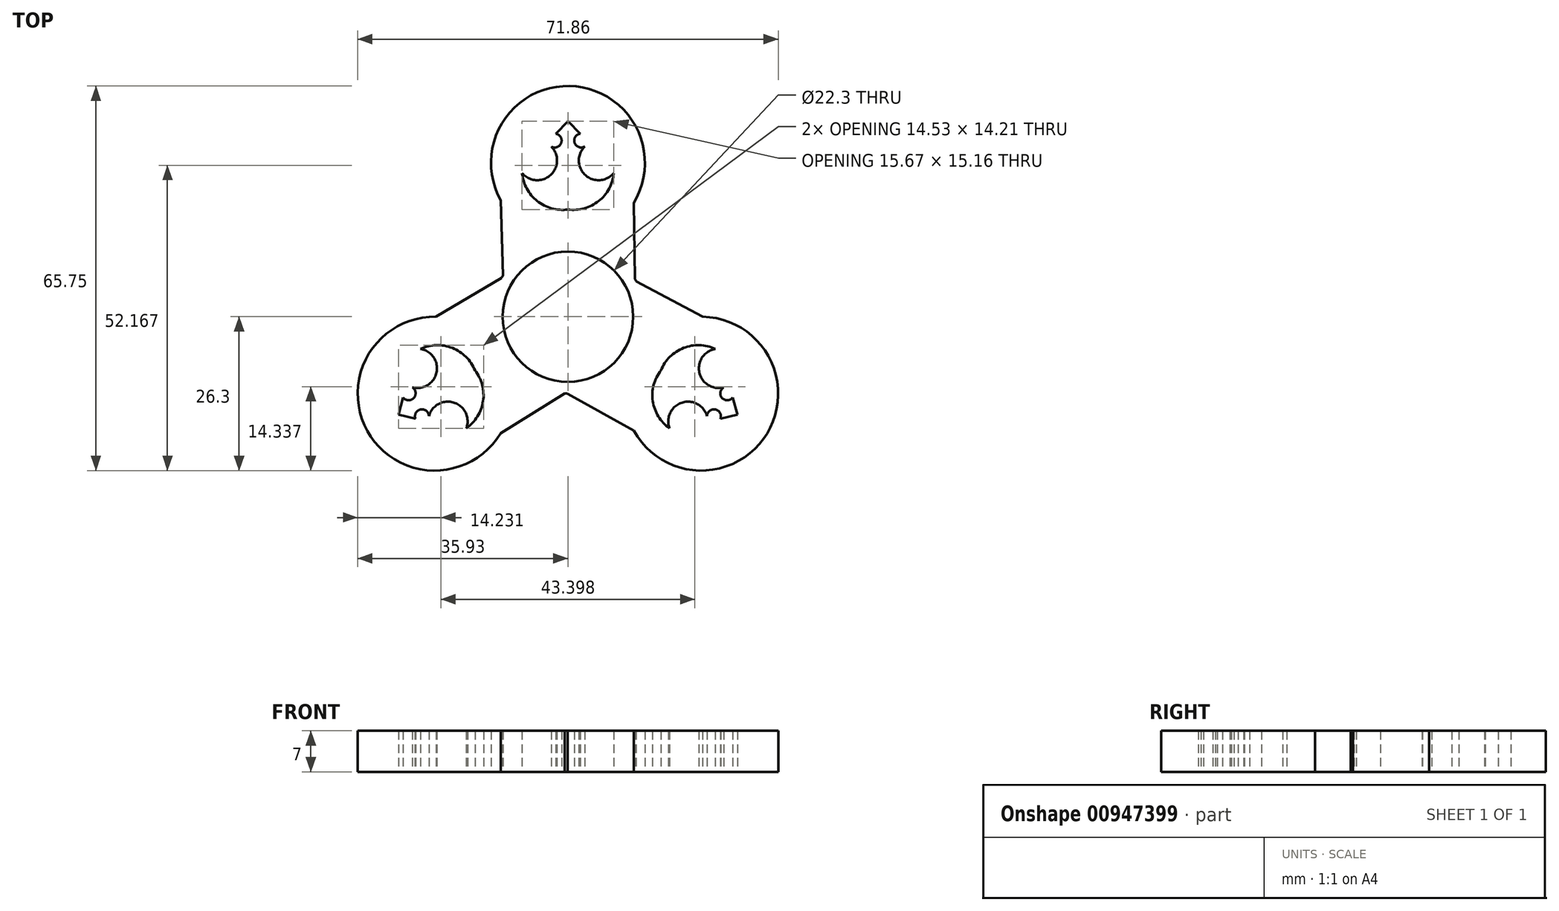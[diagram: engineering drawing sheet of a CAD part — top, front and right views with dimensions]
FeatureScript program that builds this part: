
annotation { "Feature Type Name" : "Feature", "Feature Type Description" : "" }
export const myFeature = defineFeature(function(context is Context, id is Id, definition is map)
    precondition{}
    {
        {
            var Q0;
            Q0=qCreatedBy(makeId("Top.planeOp"),FACE);
            var sketch = newSketch(context, id + "F0", { "sketchPlane" : qUnion([Q0])});
            skCircle(sketch, "E0", {"center": v(0, 0) * mm, "radius": 11.15 * mm});
            skCircle(sketch, "E1.0", {"center": v(0, 0) * mm, "radius": 13.15 * mm});
            skCircle(sketch, "E2", {"center": v(0, 26.3) * mm, "radius": 11.15 * mm});
            skCircle(sketch, "E3.0", {"center": v(0, 26.3) * mm, "radius": 13.15 * mm});
            skLineSegment(sketch, "E4", {"start": v(11.25, 19.48) * mm, "end": v(11.43, 6.5) * mm});
            skLineSegment(sketch, "E5", {"start": v(-11.5, 19.93) * mm, "end": v(-11.1, 7.06) * mm});
            skLineSegment(sketch, "E6", {"start": v(0, 33.45) * mm, "end": v(2.1, 31.3) * mm});
            skArc(sketch, "E7", {"start": v(2.1, 31.3) * mm, "mid": v(1.15, 29.74) * mm, "end": v(2.85, 29.08) * mm});
            skArc(sketch, "E8", {"start": v(2.85, 29.08) * mm, "mid": v(2.97, 24.2) * mm, "end": v(7.83, 24.57) * mm});
            skArc(sketch, "E9", {"start": v(0, 18.34) * mm, "mid": v(5.25, 19.77) * mm, "end": v(7.83, 24.57) * mm});
            skLineSegment(sketch, "E10.MirrorCS", {"start": v(0, 33.45) * mm, "end": v(-2.1, 31.3) * mm});
            skArc(sketch, "E11.MirrorCS", {"start": v(-2.1, 31.3) * mm, "mid": v(-1.15, 29.74) * mm, "end": v(-2.85, 29.08) * mm});
            skArc(sketch, "E12.MirrorCS", {"start": v(-2.85, 29.08) * mm, "mid": v(-2.97, 24.2) * mm, "end": v(-7.83, 24.57) * mm});
            skArc(sketch, "E13.MirrorCS", {"start": v(0, 18.34) * mm, "mid": v(-5.25, 19.77) * mm, "end": v(-7.83, 24.57) * mm});
            skCircle(sketch, "E14.1.0", {"center": v(-22.78, -13.15) * mm, "radius": 13.15 * mm});
            skCircle(sketch, "E14.1.1", {"center": v(-22.78, -13.15) * mm, "radius": 11.15 * mm});
            skArc(sketch, "E14.1.2", {"start": v(-26.61, -12.07) * mm, "mid": v(-22.45, -9.53) * mm, "end": v(-25.2, -5.5) * mm});
            skArc(sketch, "E14.1.3", {"start": v(-28.15, -13.82) * mm, "mid": v(-26.32, -13.88) * mm, "end": v(-26.61, -12.07) * mm});
            skLineSegment(sketch, "E14.1.4", {"start": v(-28.97, -16.72) * mm, "end": v(-28.15, -13.82) * mm});
            skLineSegment(sketch, "E14.1.5", {"start": v(-28.97, -16.72) * mm, "end": v(-26.05, -17.47) * mm});
            skArc(sketch, "E14.1.6", {"start": v(-26.05, -17.47) * mm, "mid": v(-25.18, -15.86) * mm, "end": v(-23.76, -17) * mm});
            skArc(sketch, "E14.1.7", {"start": v(-23.76, -17) * mm, "mid": v(-19.48, -14.68) * mm, "end": v(-17.36, -19.07) * mm});
            skArc(sketch, "E14.1.8", {"start": v(-15.88, -9.17) * mm, "mid": v(-19.75, -5.34) * mm, "end": v(-25.2, -5.5) * mm});
            skArc(sketch, "E14.1.9", {"start": v(-15.88, -9.17) * mm, "mid": v(-14.5, -14.43) * mm, "end": v(-17.36, -19.07) * mm});
            skLineSegment(sketch, "E14.1.10", {"start": v(-22.5, 0) * mm, "end": v(-11.35, 6.64) * mm});
            skLineSegment(sketch, "E14.1.11", {"start": v(-11.5, -19.93) * mm, "end": v(-0.56, -13.14) * mm});
            skCircle(sketch, "E14.2.0", {"center": v(22.78, -13.15) * mm, "radius": 13.15 * mm});
            skCircle(sketch, "E14.2.1", {"center": v(22.78, -13.15) * mm, "radius": 11.15 * mm});
            skArc(sketch, "E14.2.2", {"start": v(23.76, -17) * mm, "mid": v(19.48, -14.68) * mm, "end": v(17.36, -19.07) * mm});
            skArc(sketch, "E14.2.3", {"start": v(26.05, -17.47) * mm, "mid": v(25.18, -15.86) * mm, "end": v(23.76, -17) * mm});
            skLineSegment(sketch, "E14.2.4", {"start": v(28.97, -16.72) * mm, "end": v(26.05, -17.47) * mm});
            skLineSegment(sketch, "E14.2.5", {"start": v(28.97, -16.72) * mm, "end": v(28.15, -13.82) * mm});
            skArc(sketch, "E14.2.6", {"start": v(28.15, -13.82) * mm, "mid": v(26.32, -13.88) * mm, "end": v(26.61, -12.07) * mm});
            skArc(sketch, "E14.2.7", {"start": v(26.61, -12.07) * mm, "mid": v(22.45, -9.53) * mm, "end": v(25.2, -5.5) * mm});
            skArc(sketch, "E14.2.8", {"start": v(15.88, -9.17) * mm, "mid": v(14.5, -14.43) * mm, "end": v(17.36, -19.07) * mm});
            skArc(sketch, "E14.2.9", {"start": v(15.88, -9.17) * mm, "mid": v(19.75, -5.34) * mm, "end": v(25.2, -5.5) * mm});
            skLineSegment(sketch, "E14.2.10", {"start": v(11.25, -19.48) * mm, "end": v(-0.08, -13.15) * mm});
            skLineSegment(sketch, "E14.2.11", {"start": v(23.01, 0) * mm, "end": v(11.66, 6.08) * mm});
            skSolve(sketch);
        }
        {
            var Q0;
            Q0=makeQuery(id+"F0.imprint","IMPRINT",FACE,{"disambiguationData":[TD([[makeQuery(id+"F0.imprint","IMPRINT",EDGE,{"derivedFrom":sQuery(id+"F0.wireOp",EDGE,"E2")}),-1.0]])]});
            var Q1;
            Q1=makeQuery(id+"F0.imprint","IMPRINT",FACE,{"disambiguationData":[TD([[makeQuery(id+"F0.imprint","IMPRINT",EDGE,{"derivedFrom":sQuery(id+"F0.wireOp",EDGE,"E2")}),1.0]])]});
            var Q2;
            {var subQ0=sQuery(id+"F0.wireOp",EDGE,"E4");Q2=makeQuery(id+"F0.imprint","IMPRINT",FACE,{"disambiguationData":[TD([[makeQuery(id+"F0.imprint","IMPRINT",EDGE,{"derivedFrom":subQ0}),-1.0]])]});}
            var Q3;
            {var subQ0=sQuery(id+"F0.wireOp",EDGE,"E5");Q3=makeQuery(id+"F0.imprint","IMPRINT",FACE,{"disambiguationData":[TD([[makeQuery(id+"F0.imprint","IMPRINT",EDGE,{"derivedFrom":subQ0}),1.0]])]});}
            var Q4;
            Q4=makeQuery(id+"F0.imprint","IMPRINT",FACE,{"disambiguationData":[TD([[makeQuery(id+"F0.imprint","IMPRINT",EDGE,{"derivedFrom":sQuery(id+"F0.wireOp",EDGE,"E0")}),-1.0]])]});
            var Q5;
            {var subQ0=sQuery(id+"F0.wireOp",EDGE,"E14.2.11");Q5=makeQuery(id+"F0.imprint","IMPRINT",FACE,{"disambiguationData":[TD([[makeQuery(id+"F0.imprint","IMPRINT",EDGE,{"derivedFrom":subQ0}),1.0]])]});}
            var Q6;
            Q6=makeQuery(id+"F0.imprint","IMPRINT",FACE,{"disambiguationData":[TD([[makeQuery(id+"F0.imprint","IMPRINT",EDGE,{"derivedFrom":sQuery(id+"F0.wireOp",EDGE,"E14.2.1")}),-1.0]])]});
            var Q7;
            {var subQ0=sQuery(id+"F0.wireOp",EDGE,"E14.2.10");Q7=makeQuery(id+"F0.imprint","IMPRINT",FACE,{"disambiguationData":[TD([[makeQuery(id+"F0.imprint","IMPRINT",EDGE,{"derivedFrom":subQ0}),-1.0]])]});}
            var Q8;
            Q8=makeQuery(id+"F0.imprint","IMPRINT",FACE,{"disambiguationData":[TD([[makeQuery(id+"F0.imprint","IMPRINT",EDGE,{"derivedFrom":sQuery(id+"F0.wireOp",EDGE,"E14.2.1")}),1.0]])]});
            var Q9;
            {var subQ0=sQuery(id+"F0.wireOp",EDGE,"E14.1.10");Q9=makeQuery(id+"F0.imprint","IMPRINT",FACE,{"disambiguationData":[TD([[makeQuery(id+"F0.imprint","IMPRINT",EDGE,{"derivedFrom":subQ0}),-1.0]])]});}
            var Q10;
            {var subQ0=sQuery(id+"F0.wireOp",EDGE,"E14.1.11");Q10=makeQuery(id+"F0.imprint","IMPRINT",FACE,{"disambiguationData":[TD([[makeQuery(id+"F0.imprint","IMPRINT",EDGE,{"derivedFrom":subQ0}),1.0]])]});}
            var Q11;
            Q11=makeQuery(id+"F0.imprint","IMPRINT",FACE,{"disambiguationData":[TD([[makeQuery(id+"F0.imprint","IMPRINT",EDGE,{"derivedFrom":sQuery(id+"F0.wireOp",EDGE,"E14.1.1")}),-1.0]])]});
            var Q12;
            Q12=makeQuery(id+"F0.imprint","IMPRINT",FACE,{"disambiguationData":[TD([[makeQuery(id+"F0.imprint","IMPRINT",EDGE,{"derivedFrom":sQuery(id+"F0.wireOp",EDGE,"E14.1.1")}),1.0]])]});
            extrude(context, id + "F1", {"entities" : qUnion([Q0, Q1, Q2, Q3, Q4, Q5, Q6, Q7, Q8, Q9, Q10, Q11, Q12]), "depth" : 7 * mm, "offsetDistance" : 25 * mm});
        }
    });
